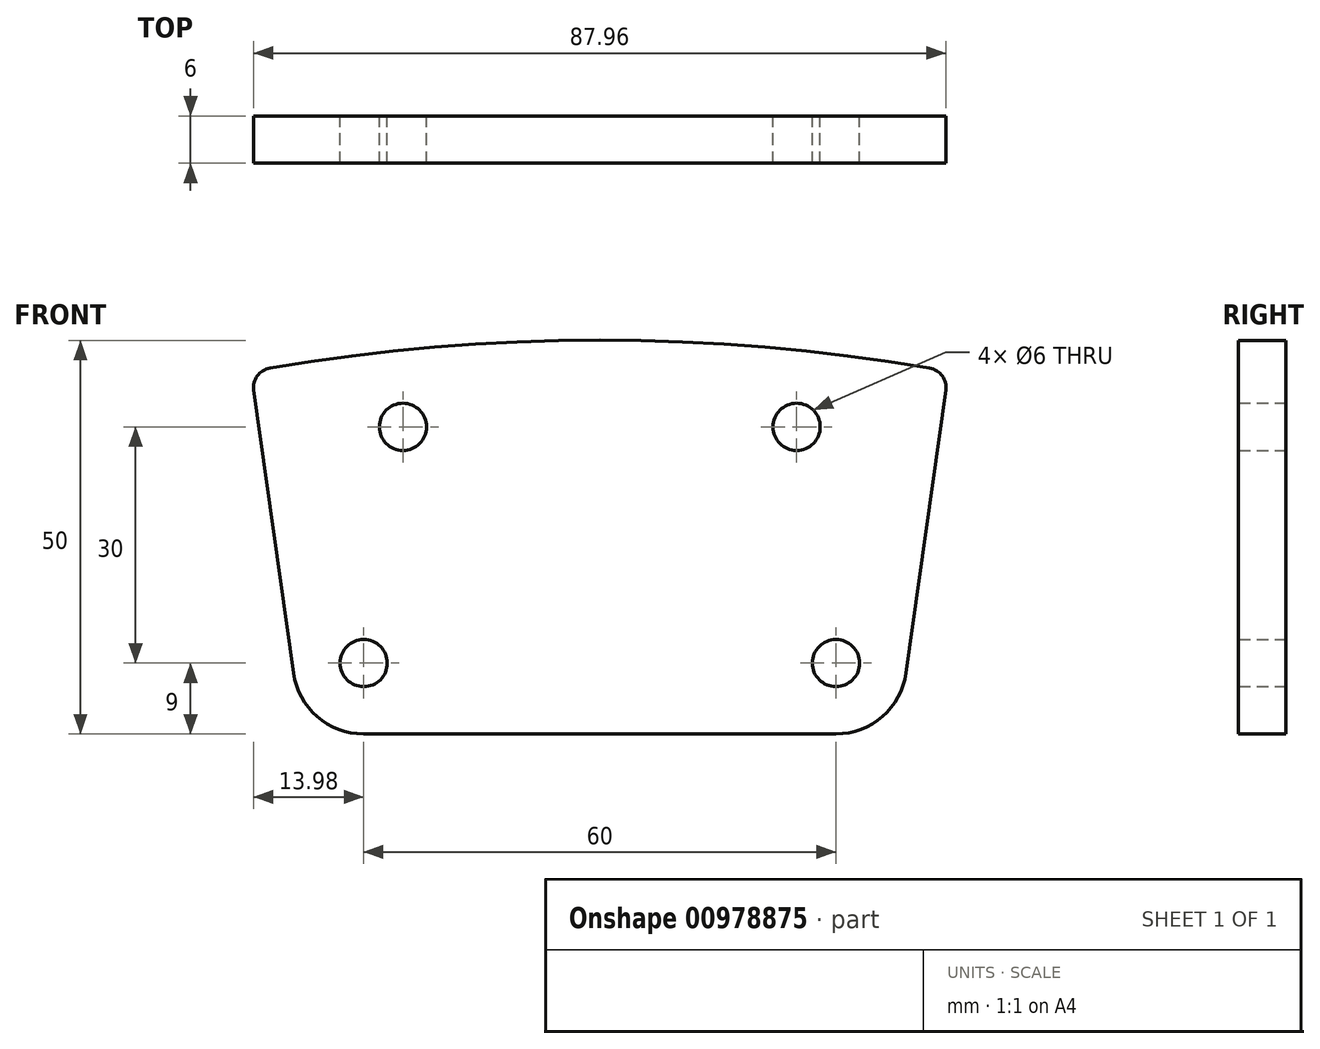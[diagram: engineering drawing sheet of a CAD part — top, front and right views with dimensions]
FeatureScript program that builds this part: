
annotation { "Feature Type Name" : "Feature", "Feature Type Description" : "" }
export const myFeature = defineFeature(function(context is Context, id is Id, definition is map)
    precondition{}
    {
        {
            var Q0;
            Q0=qCreatedBy(makeId("Front.planeOp"),FACE);
            var sketch = newSketch(context, id + "F0", { "sketchPlane" : qUnion([Q0])});
            skCircle(sketch, "E0", {"center": v(-25, 30) * mm, "radius": 3 * mm});
            skCircle(sketch, "E1", {"center": v(25, 30) * mm, "radius": 3 * mm});
            skArc(sketch, "E2", {"start": v(30, -9) * mm, "mid": v(35.9, -6.8) * mm, "end": v(38.91, -1.25) * mm});
            skArc(sketch, "E3", {"start": v(-38.91, -1.25) * mm, "mid": v(-35.9, -6.8) * mm, "end": v(-30, -9) * mm});
            skLineSegment(sketch, "E4", {"start": v(-30, -9) * mm, "end": v(30, -9) * mm});
            skLineSegment(sketch, "E5", {"start": v(38.91, -1.25) * mm, "end": v(43.96, 34.65) * mm});
            skLineSegment(sketch, "E6", {"start": v(-38.91, -1.25) * mm, "end": v(-43.96, 34.65) * mm});
            skCircle(sketch, "E7", {"center": v(-30, 0) * mm, "radius": 3 * mm});
            skCircle(sketch, "E8", {"center": v(30, 0) * mm, "radius": 3 * mm});
            skArc(sketch, "E9", {"start": v(41.9, 37.46) * mm, "mid": v(0, 41) * mm, "end": v(-41.9, 37.46) * mm});
            skPoint(sketch, "E10.visualSharp", {"position": v(-44.3, 37.04) * mm});
            skArc(sketch, "E10.filletArc", {"start": v(-41.9, 37.46) * mm, "mid": v(-43.5, 36.47) * mm, "end": v(-43.96, 34.65) * mm});
            skPoint(sketch, "E11.visualSharp", {"position": v(44.3, 37.04) * mm});
            skArc(sketch, "E11.filletArc", {"start": v(43.96, 34.65) * mm, "mid": v(43.5, 36.47) * mm, "end": v(41.9, 37.46) * mm});
            skSolve(sketch);
        }
        {
            var Q0;
            Q0 = qSketchRegion(id + "F0", true);
            extrude(context, id + "F1", {"entities" : qUnion([Q0]), "depth" : 6 * mm, "offsetDistance" : 25 * mm});
        }
    });
